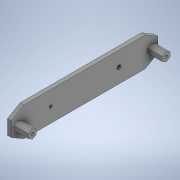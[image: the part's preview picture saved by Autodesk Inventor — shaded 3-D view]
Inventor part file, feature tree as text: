
AUTODESK INVENTOR PART (.ipt)
format: ipt  version: 2020 (Build 240168000, 168)  size: 258,048 bytes
history: native  units: in
note: dims shown in document units (in); Inventor stores cm internally (conversion verified against a paired STEP export)
features: extrude x7, sketch x7, plane x1
ambient origin geometry x8: Origin, YZ Plane, XZ Plane, XY Plane, X Axis, Y Axis, Z Axis, Center Point
bodies: Solid1 (feature_tree)
feature tree (15):
  extrude  "Extrusion1"  Depth=5.9055in
  extrude  "Extrusion3"  TaperAngle=0.0deg  [1 undecoded]
  extrude  "Extrusion4"  Depth=0.5906in
  plane  "Work Plane1"
  extrude  "Extrusion5"  Depth=0.122in
  extrude  "Extrusion6"  Depth=0.2402in
  extrude  "Extrusion7"  [1 undecoded]
  extrude  "Extrusion8"  Depth=0.0866in TaperAngle=0.0deg
  sketch  "Sketch1"  dims[d0=1.1811in d1=5.9055in]
  sketch  "Sketch2"  dims[d2=0.1575in d3=0.0in]
  sketch  "Sketch3"  dims[d8=0.315in d9=0.5906in]
  sketch  "Sketch4"  dims[d10=0.0in d12=0.122in]
  sketch  "Sketch5"  dims[d13=0.0in d14=0.0in d15=0.2402in]
  sketch  "Sketch8"  dims[d16=0.0866in d17=-0.2233in]
  sketch  "Sketch9"  dims[d18=-0.3937in d19=0.0866in d20=0.0in d26=1.5748in d27=0.1654in d28=0.122in d29=1.5748in d30=0.0in d31=0.0in d32=0.2402in d33=0.0866in d34=-0.2233in]
note: 2 required parameter values undecoded (feature->parameter linkage not recoverable at this tier; creation-order binding heuristic only, values carry confidence <= 0.55)
